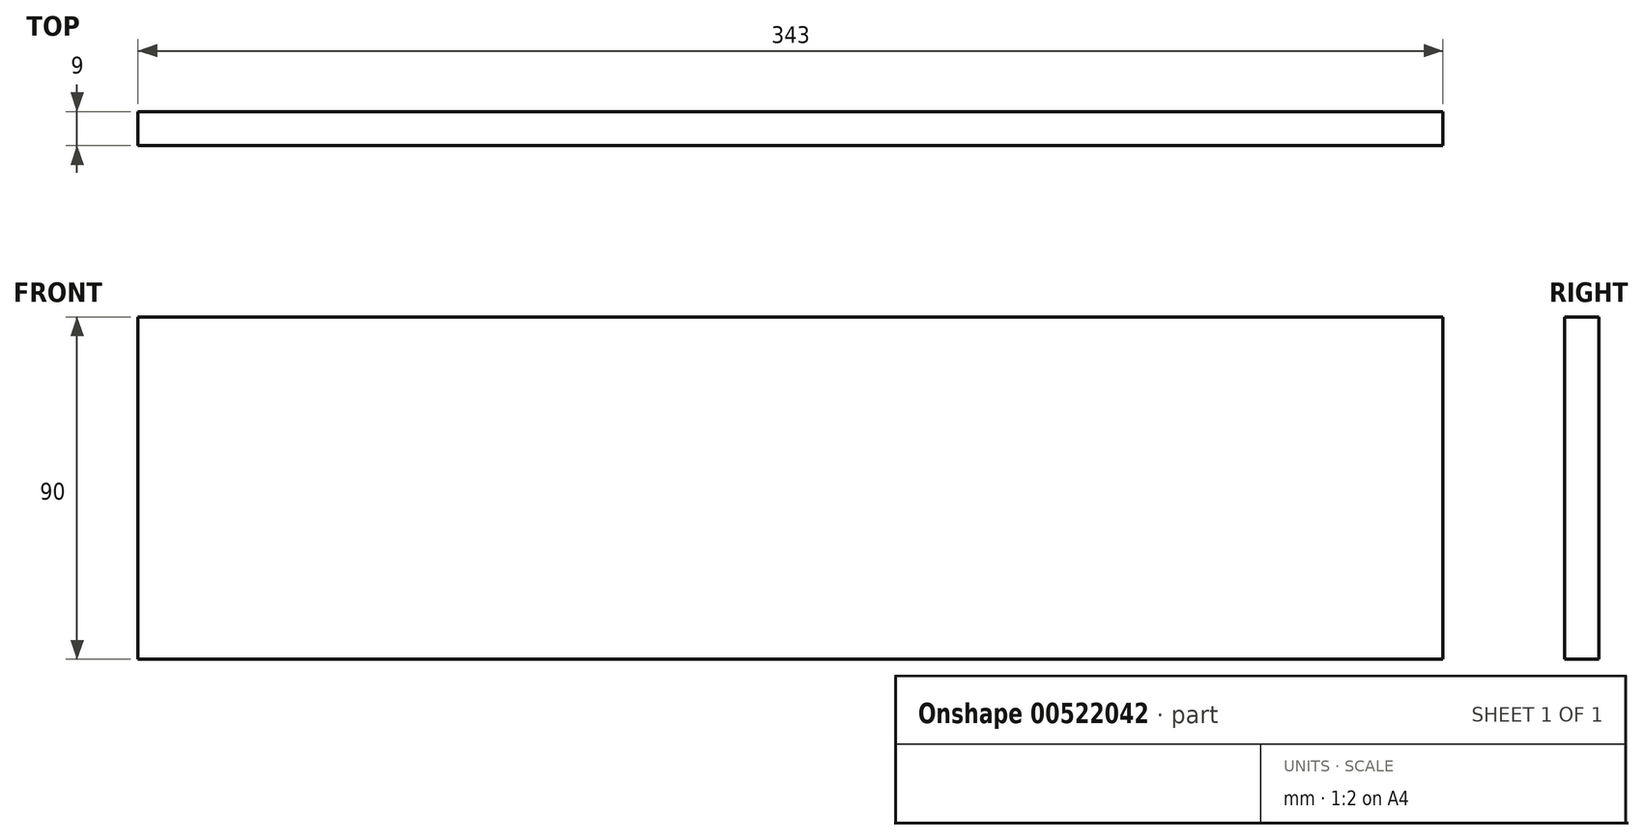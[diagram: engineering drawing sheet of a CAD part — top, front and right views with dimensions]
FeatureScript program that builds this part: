
annotation { "Feature Type Name" : "Feature", "Feature Type Description" : "" }
export const myFeature = defineFeature(function(context is Context, id is Id, definition is map)
    precondition{}
    {
        {
            var Q0;
            Q0=qCreatedBy(makeId("Front.planeOp"),FACE);
            var sketch = newSketch(context, id + "F0", { "sketchPlane" : qUnion([Q0])});
            skLineSegment(sketch, "E0.bottom", {"start": v(0, 0) * mm, "end": v(-343, 0) * mm});
            skLineSegment(sketch, "E0.top", {"start": v(0, 90) * mm, "end": v(-343, 90) * mm});
            skLineSegment(sketch, "E0.left", {"start": v(0, 0) * mm, "end": v(0, 90) * mm});
            skLineSegment(sketch, "E0.right", {"start": v(-343, 0) * mm, "end": v(-343, 90) * mm});
            skSolve(sketch);
        }
        {
            var Q0;
            Q0=makeQuery(id+"F0.imprint","IMPRINT",FACE,{"disambiguationData":[TD([[makeQuery(id+"F0.imprint","IMPRINT",EDGE,{"derivedFrom":sQuery(id+"F0.wireOp",EDGE,"E0.bottom")}),-1.0]])]});
            extrude(context, id + "F1", {"entities" : qUnion([Q0]), "depth" : 9 * mm, "offsetDistance" : 25 * mm});
        }
    });
